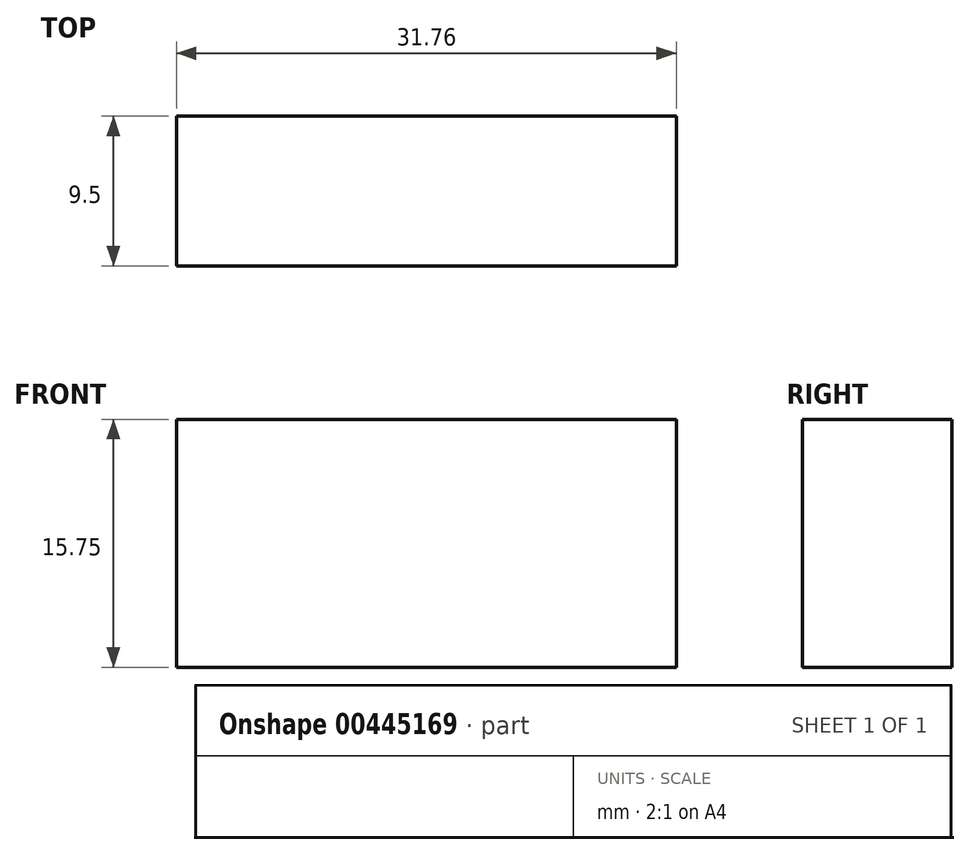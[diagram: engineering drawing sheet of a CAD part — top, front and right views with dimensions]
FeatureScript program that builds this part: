
annotation { "Feature Type Name" : "Feature", "Feature Type Description" : "" }
export const myFeature = defineFeature(function(context is Context, id is Id, definition is map)
    precondition{}
    {
        {
            var Q0;
            Q0=qCreatedBy(makeId("Top.planeOp"),FACE);
            var sketch = newSketch(context, id + "F0", { "sketchPlane" : qUnion([Q0])});
            skLineSegment(sketch, "E0.bottom", {"start": v(15.88, 4.75) * mm, "end": v(-15.88, 4.75) * mm});
            skLineSegment(sketch, "E0.top", {"start": v(15.88, -4.75) * mm, "end": v(-15.87, -4.75) * mm});
            skLineSegment(sketch, "E0.left", {"start": v(15.88, 4.75) * mm, "end": v(15.88, -4.75) * mm});
            skLineSegment(sketch, "E0.right", {"start": v(-15.88, 4.75) * mm, "end": v(-15.87, -4.75) * mm});
            skPoint(sketch, "E0.middle", {"position": v(0, 0) * mm});
            skSolve(sketch);
        }
        {
            var Q0;
            Q0 = qSketchRegion(id + "F0", true);
            extrude(context, id + "F1", {"entities" : qUnion([Q0]), "depth" : 15.75 * mm});
        }
    });
